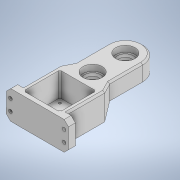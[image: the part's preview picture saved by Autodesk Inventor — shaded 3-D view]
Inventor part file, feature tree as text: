
AUTODESK INVENTOR PART (.ipt)
format: ipt  version: 2021 (Build 250183000, 183)  size: 319,488 bytes
history: native  units: mm
features: sketch x7, extrude x6, chamfer x6, plane x1
ambient origin geometry x8: Origin, YZ Plane, XZ Plane, XY Plane, X Axis, Y Axis, Z Axis, Center Point
bodies: Solid1 (feature_tree)
feature tree (20):
  extrude  "Extrusion1"  Depth=22.4mm
  plane  "Work Plane1"
  extrude  "Extrusion2"  Depth=38.0mm
  chamfer  "Chamfer1"  Distance=21.0mm
  extrude  "Extrusion3"  Depth=14.0mm
  extrude  "Extrusion4"  Depth=7.0mm TaperAngle=0.0deg
  chamfer  "Chamfer2"  Distance=2.0mm Angle=45.0deg
  extrude  "Extrusion5"  Depth=42.2mm
  extrude  "Extrusion6"  Depth=0.1mm
  chamfer  "Chamfer3"  Distance=21.1mm
  chamfer  "Chamfer4"  Distance=23.0mm
  sketch  "Sketch7"  dims[d16=42.2mm d17=42.2mm d18=21.1mm d19=21.1mm d20=23.0mm d21=0.0mm d22=38.0mm d23=5.0mm d24=7.0mm d25=0.0mm d26=3.0mm d27=3.0mm d28=3.0mm d29=3.0mm d30=31.5mm d31=31.5mm d32=31.5mm d33=31.5mm d34=5.35mm d35=5.35mm d36=5.35mm d37=5.35mm d38=23.0mm d39=21.1mm d40=21.1mm d41=5.0mm d42=0.0mm d43=11.9mm d44=2.0mm d45=45.0deg d47=4.2mm d48=4.2mm d52=10.0mm d54=4.2mm d55=4.2mm d59=10.0mm d60=8.0mm d61=0.0mm d62=7.0mm d63=7.0mm d64=7.0mm d65=7.0mm d66=4.0mm d67=0.0mm d68=5.0mm d69=2.0mm d70=45.0deg d71=2.0mm d72=2.0mm d73=45.0deg d74=0.1mm d75=2.0mm d76=45.0deg d77=2.0mm d78=2.0mm d79=45.0deg]
  chamfer  "Chamfer5"  [1 undecoded]
  chamfer  "Chamfer6"  Distance=38.0mm
  sketch  "Sketch1"  dims[d0=22.4mm d1=22.4mm]
  sketch  "Sketch2"  dims[d2=0.0mm d3=38.0mm]
  sketch  "Sketch3"  dims[d4=40.0mm]
  sketch  "Sketch4"  dims[d5=40.0mm d6=21.0mm d7=0.0mm]
  sketch  "Sketch5"  dims[d8=-7.0mm d9=14.0mm]
  sketch  "Sketch6"  dims[d10=14.0mm d11=7.0mm d12=0.0mm d13=2.0mm d14=2.0mm d15=45.0deg]
note: 1 required parameter value undecoded (feature->parameter linkage not recoverable at this tier; creation-order binding heuristic only, values carry confidence <= 0.55)
